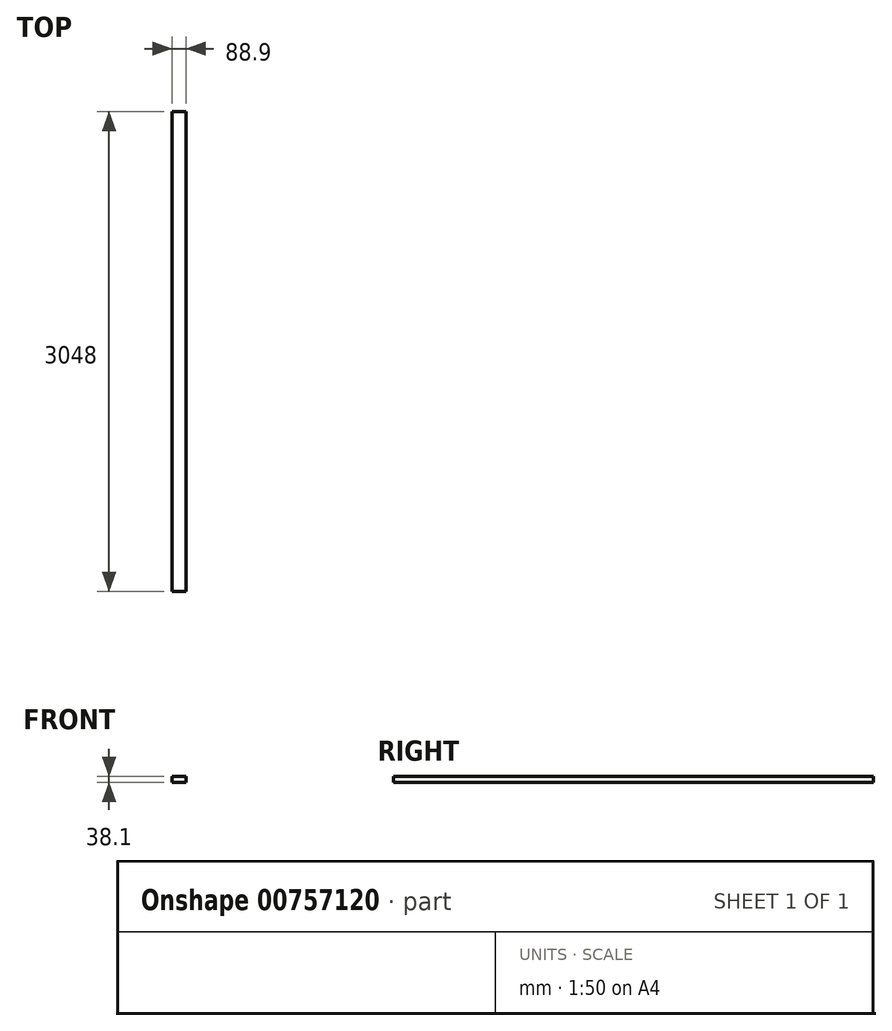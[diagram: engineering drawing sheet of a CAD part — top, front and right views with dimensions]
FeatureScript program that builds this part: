
annotation { "Feature Type Name" : "Feature", "Feature Type Description" : "" }
export const myFeature = defineFeature(function(context is Context, id is Id, definition is map)
    precondition{}
    {
        {
            var Q0;
            Q0=qCreatedBy(makeId("Front.planeOp"),FACE);
            var sketch = newSketch(context, id + "F0", { "sketchPlane" : qUnion([Q0])});
            skLineSegment(sketch, "E0.bottom", {"start": v(0, 0) * mm, "end": v(88.9, 0) * mm});
            skLineSegment(sketch, "E0.top", {"start": v(0, 38.1) * mm, "end": v(88.9, 38.1) * mm});
            skLineSegment(sketch, "E0.left", {"start": v(0, 0) * mm, "end": v(0, 38.1) * mm});
            skLineSegment(sketch, "E0.right", {"start": v(88.9, 0) * mm, "end": v(88.9, 38.1) * mm});
            skSolve(sketch);
        }
        {
            var Q0;
            Q0=makeQuery(id+"F0.imprint","IMPRINT",FACE,{"disambiguationData":[TD([[makeQuery(id+"F0.imprint","IMPRINT",EDGE,{"derivedFrom":sQuery(id+"F0.wireOp",EDGE,"E0.bottom")}),1.0]])]});
            extrude(context, id + "F1", {"entities" : qUnion([Q0]), "depth" : 3048 * mm, "offsetDistance" : 25.4 * mm});
        }
    });
